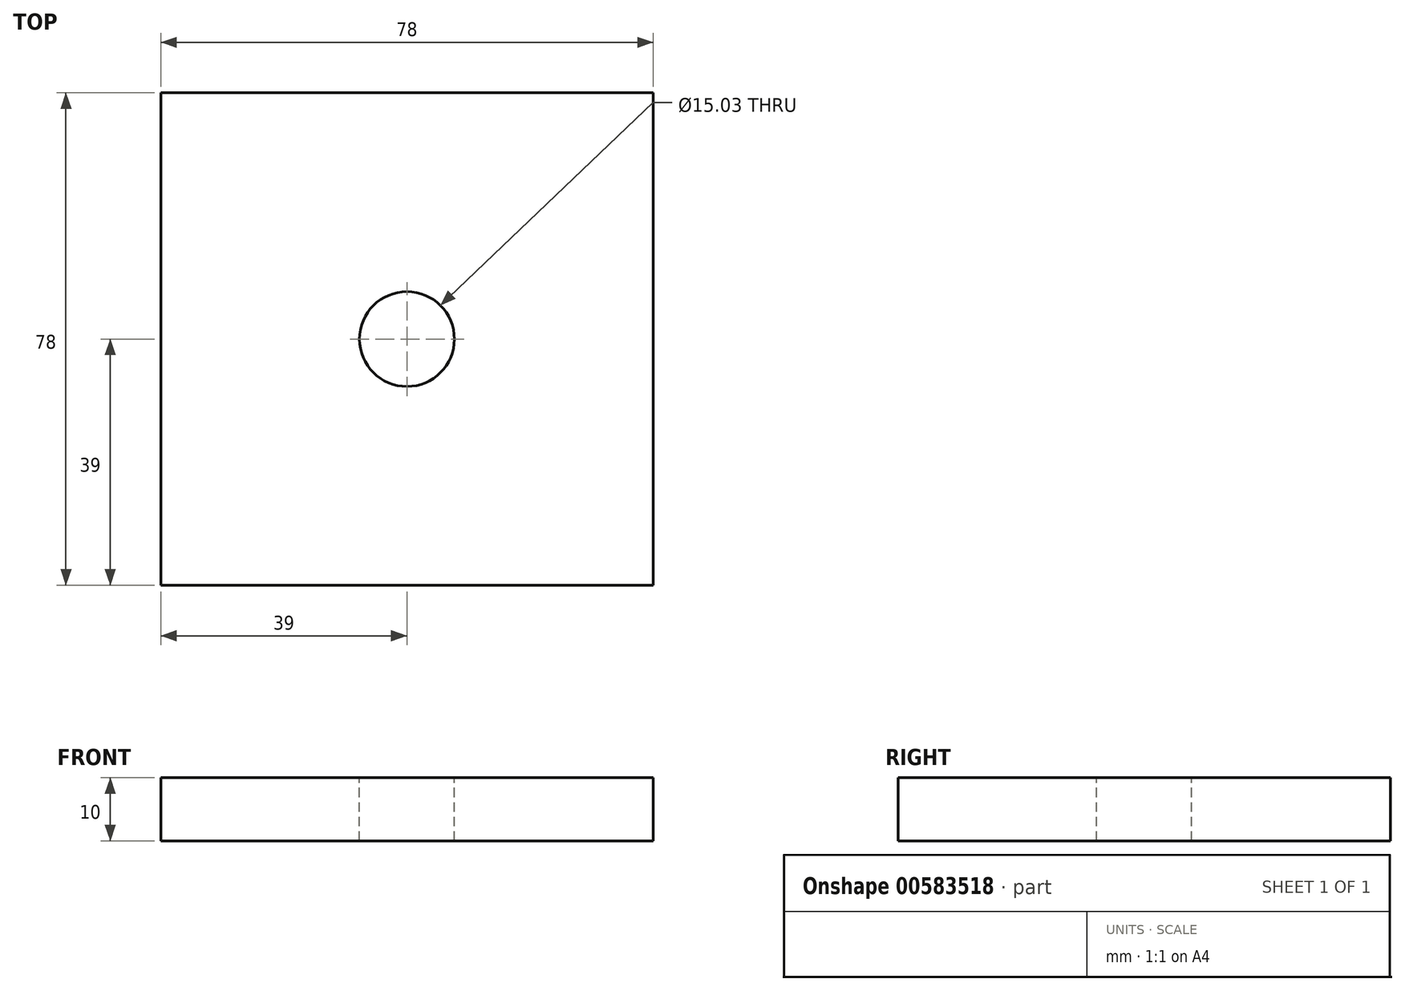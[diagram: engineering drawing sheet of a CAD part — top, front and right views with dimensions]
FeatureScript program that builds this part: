
annotation { "Feature Type Name" : "Feature", "Feature Type Description" : "" }
export const myFeature = defineFeature(function(context is Context, id is Id, definition is map)
    precondition{}
    {
        {
            var Q0;
            Q0=qCreatedBy(makeId("Top.planeOp"),FACE);
            var sketch = newSketch(context, id + "F0", { "sketchPlane" : qUnion([Q0])});
            skLineSegment(sketch, "E0.bottom", {"start": v(39, -39) * mm, "end": v(-39, -39) * mm});
            skLineSegment(sketch, "E0.top", {"start": v(39, 39) * mm, "end": v(-39, 39) * mm});
            skLineSegment(sketch, "E0.left", {"start": v(39, -39) * mm, "end": v(39, 39) * mm});
            skLineSegment(sketch, "E0.right", {"start": v(-39, -39) * mm, "end": v(-39, 39) * mm});
            skPoint(sketch, "E0.middle", {"position": v(0, 0) * mm});
            skSolve(sketch);
        }
        {
            var Q0;
            Q0=makeQuery(id+"F0.imprint","IMPRINT",FACE,{"disambiguationData":[TD([[makeQuery(id+"F0.imprint","IMPRINT",EDGE,{"derivedFrom":sQuery(id+"F0.wireOp",EDGE,"E0.bottom")}),-1.0]])]});
            extrude(context, id + "F1", {"entities" : qUnion([Q0]), "depth" : 10 * mm, "offsetDistance" : 25 * mm});
        }
        {
            var Q0;
            Q0=makeQuery(id+"F1.opExtrude","CAP_FACE",FACE,{"disambiguationData":[OSD([sQuery(id+"F0.wireOp",EDGE,"E0.bottom"),sQuery(id+"F0.wireOp",EDGE,"E0.top"),sQuery(id+"F0.wireOp",EDGE,"E0.left"),sQuery(id+"F0.wireOp",EDGE,"E0.right")])],"isStart":false});
            var sketch = newSketch(context, id + "F2", { "sketchPlane" : qUnion([Q0])});
            skCircle(sketch, "E1", {"center": v(0, 0) * mm, "radius": 7.51 * mm});
            skSolve(sketch);
        }
        {
            var Q0;
            Q0 = qSketchRegion(id + "F2", true);
            extrude(context, id + "F3", {"entities" : qUnion([Q0]), "operationType" : NewBodyOperationType.REMOVE, "oppositeDirection" : true, "depth" : 25 * mm, "offsetDistance" : 25 * mm});
        }
    });
